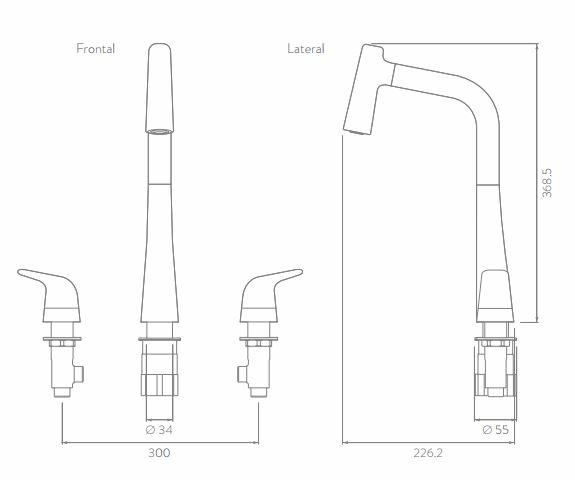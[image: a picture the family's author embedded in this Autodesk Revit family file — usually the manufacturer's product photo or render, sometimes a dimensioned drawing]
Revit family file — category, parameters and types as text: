
# Revit family: LQ5000001_Griferia para Lavaplatos Liquid Niquel
name_source: partatom
category: Plumbing Fixtures
units: mm (PartAtom-declared; Revit-internal decimal feet)

## family parameters
Cut with Voids When Loaded = No
Host = Face
OmniClass Number = 23.31.11.00
OmniClass Title = Faucets
Part Type = Normal
Room Calculation Point = No
Round Connector Dimension = Use Diameter
Shared = No

## types (2) — shared parameters
Actual Estimated Flow Capacity at 60 psi = 5,6 L/min.
CW Connection = Yes
Creado por = IDD
Default Elevation = 1219 mm
Depth = 226 mm  [stored 0.74147 ft]
Description = La línea de griferías, duchas y accesorios Liquid se inspira en la tensión superficial del agua
y en cómo esta crea formas armoniosas adaptándose al ambiente. Al igual que el agua,
las superficies de las griferías Liquid juegan con la luz y los reflejos que fluyen alrededor
de sus formas, sus líneas continuas y simplicidad formal proporcionan la ventaja práctica,
limpieza sin esfuerzo
Drain Diameter = 15 mm  [stored 0.0492126 ft]
Fabrication place = Colombia
Fecha de creación = 13/10/2020
Gross Weight = 2.600 g. - 5,73 lb.
HW Connection = Yes
Height = 368 mm  [stored 1.20735 ft]
Manufacturer = Corona
Maximum Pressure = 125 psi (860 Kpa).
Maximum Working Temperature = 71°C / 159,8°F
Minimum Pressure = 20 psi (140 Kpa).
Minimum Working Temperature = 5°C / 41 °F
Model = Lavaplatos Monocontrol Liquid
Net Weight = .350 g. - 5,18 lb.
Reference = LQ5010001
Service Life or Wear (Unit) = 500.000 ciclos.
Tecnologías = DuraCrome, EcoStream, ThermoControl
URL = https://corona.co
Uso = Residencial
Warranty = 30 años
Waste Connection = Yes
Weight = 2500 g
Width = 55 mm

## per-type parameters (varying)
| type | Acabado | Material |
| Cromo | Corona_Niquel | Corona_Metálico |
| Niquel | <By Category> | <By Category> |

note: [stored X ft] marks values corroborated as IEEE doubles in the binary element streams (Revit-internal decimal feet)

## geometry (parser evidence)
native form markers: Blend x4, Extrusion x1, Sweep x17
no freeform markers — native parametric forms only
